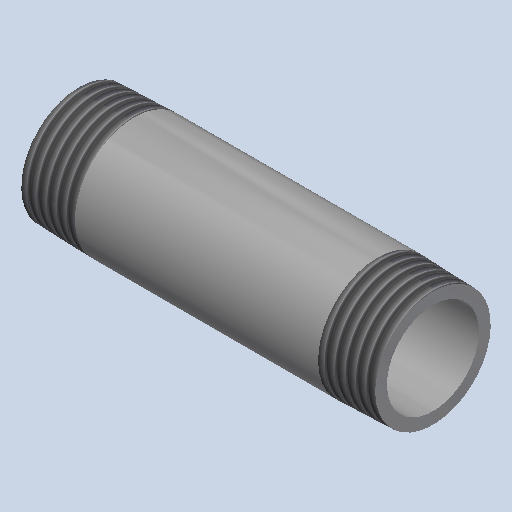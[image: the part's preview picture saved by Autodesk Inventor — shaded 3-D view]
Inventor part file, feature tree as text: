
AUTODESK INVENTOR PART (.ipt)
format: ipt  version: 2025 (Build 290162000, 162)  size: 221,184 bytes
history: native  units: mm (DEFAULTED — no unit token found)
features: other x8, revolve x1
ambient origin geometry x8: Origin, YZ Plane, XZ Plane, XY Plane, X Axis, Y Axis, Z Axis, Center Point
bodies: Solid1 (feature_tree)
feature tree (9):
  revolve  "Revolution1"  [1 undecoded]
  other  "Work Axis1"
  other  "Work Point5"
  other  "Work Axis2"
  other  "Work Point6"
  other  "Work Axis3"
  other  "Work Axis4"
  other  "Work Point7"
  other  "Work Point8"
note: 1 required parameter value undecoded (feature->parameter linkage not recoverable at this tier; creation-order binding heuristic only, values carry confidence <= 0.55)
